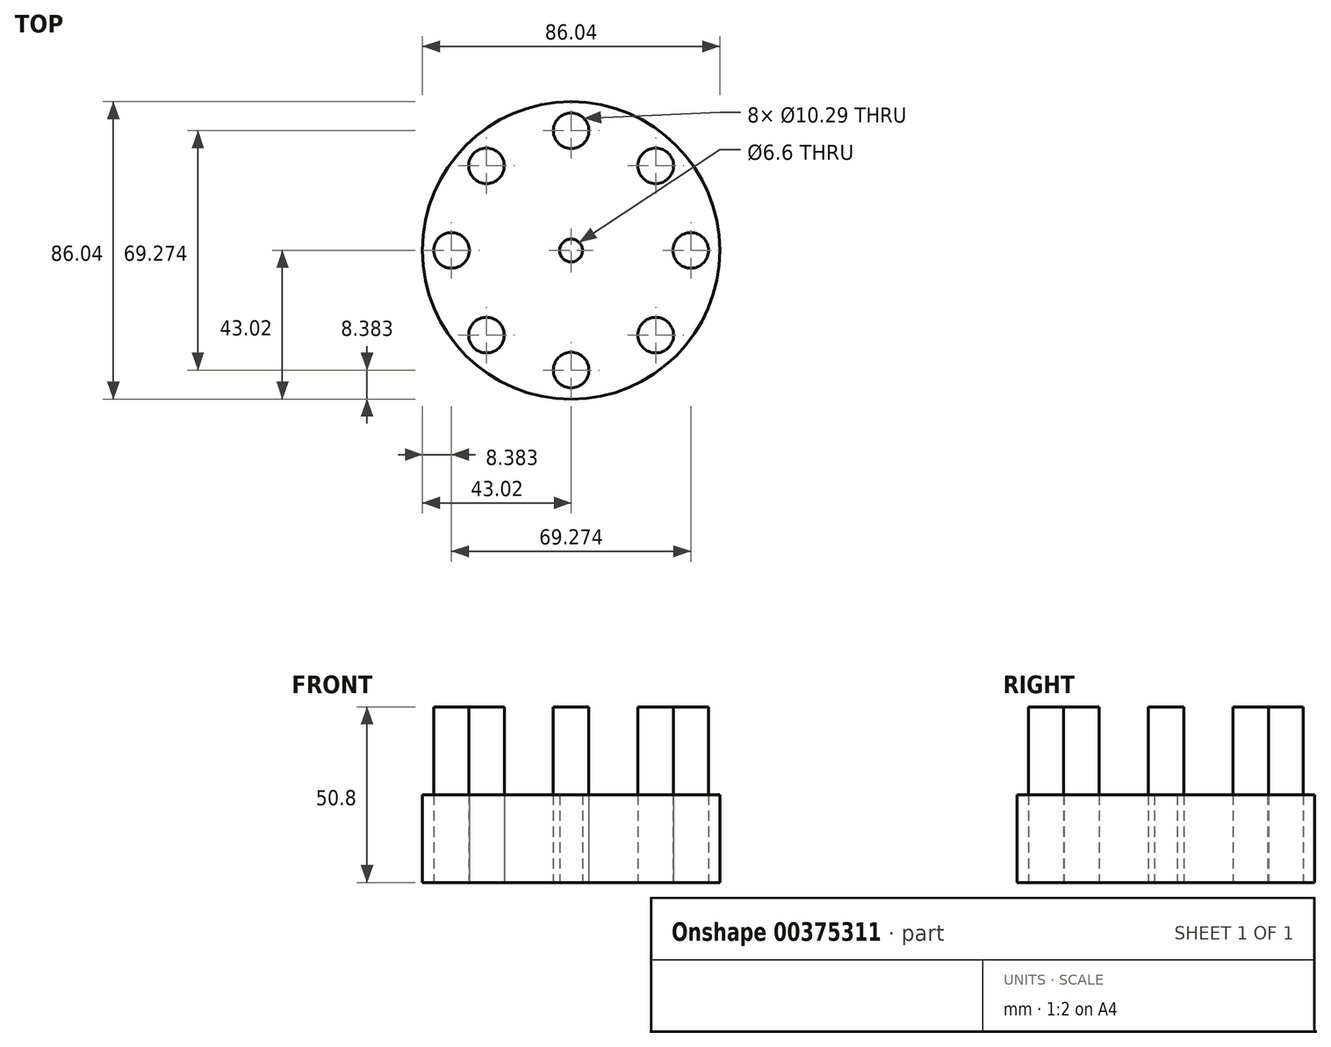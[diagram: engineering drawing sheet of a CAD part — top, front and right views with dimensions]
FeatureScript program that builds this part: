
annotation { "Feature Type Name" : "Feature", "Feature Type Description" : "" }
export const myFeature = defineFeature(function(context is Context, id is Id, definition is map)
    precondition{}
    {
        {
            var Q0;
            Q0=qCreatedBy(makeId("Top.planeOp"),FACE);
            var sketch = newSketch(context, id + "F0", { "sketchPlane" : qUnion([Q0])});
            skCircle(sketch, "E0", {"center": v(0, 0) * mm, "radius": 43.02 * mm});
            skLineSegment(sketch, "E1", {"start": v(0, 43.02) * mm, "end": v(0, 34.64) * mm, "construction": true});
            skCircle(sketch, "E2", {"center": v(0, 34.64) * mm, "radius": 5.15 * mm});
            skCircle(sketch, "E3.1.0", {"center": v(-24.5, 24.5) * mm, "radius": 5.15 * mm});
            skCircle(sketch, "E3.2.0", {"center": v(-34.64, 0) * mm, "radius": 5.15 * mm});
            skCircle(sketch, "E3.3.0", {"center": v(-24.5, -24.5) * mm, "radius": 5.15 * mm});
            skCircle(sketch, "E3.4.0", {"center": v(0, -34.64) * mm, "radius": 5.15 * mm});
            skCircle(sketch, "E3.5.0", {"center": v(24.5, -24.5) * mm, "radius": 5.15 * mm});
            skCircle(sketch, "E3.6.0", {"center": v(34.64, 0) * mm, "radius": 5.15 * mm});
            skCircle(sketch, "E3.7.0", {"center": v(24.5, 24.5) * mm, "radius": 5.15 * mm});
            skCircle(sketch, "E4", {"center": v(0, 0) * mm, "radius": 3.3 * mm});
            skSolve(sketch);
        }
        {
            var Q0;
            Q0=makeQuery(id+"F0.imprint","IMPRINT",FACE,{"disambiguationData":[TD([[makeQuery(id+"F0.imprint","IMPRINT",EDGE,{"derivedFrom":sQuery(id+"F0.wireOp",EDGE,"E2")}),1.0]])]});
            extrude(context, id + "F1", {"entities" : qUnion([Q0]), "depth" : 50.8 * mm});
        }
        {
            var Q0;
            Q0=makeQuery(id+"F0.imprint","IMPRINT",FACE,{"disambiguationData":[TD([[makeQuery(id+"F0.imprint","IMPRINT",EDGE,{"derivedFrom":sQuery(id+"F0.wireOp",EDGE,"E3.1.0")}),1.0]])]});
            extrude(context, id + "F2", {"entities" : qUnion([Q0]), "depth" : 50.8 * mm});
        }
        {
            var Q0;
            Q0=makeQuery(id+"F0.imprint","IMPRINT",FACE,{"disambiguationData":[TD([[makeQuery(id+"F0.imprint","IMPRINT",EDGE,{"derivedFrom":sQuery(id+"F0.wireOp",EDGE,"E3.2.0")}),1.0]])]});
            extrude(context, id + "F3", {"entities" : qUnion([Q0]), "depth" : 50.8 * mm});
        }
        {
            var Q0;
            Q0=makeQuery(id+"F0.imprint","IMPRINT",FACE,{"disambiguationData":[TD([[makeQuery(id+"F0.imprint","IMPRINT",EDGE,{"derivedFrom":sQuery(id+"F0.wireOp",EDGE,"E3.3.0")}),1.0]])]});
            extrude(context, id + "F4", {"entities" : qUnion([Q0]), "depth" : 50.8 * mm});
        }
        {
            var Q0;
            Q0=makeQuery(id+"F0.imprint","IMPRINT",FACE,{"disambiguationData":[TD([[makeQuery(id+"F0.imprint","IMPRINT",EDGE,{"derivedFrom":sQuery(id+"F0.wireOp",EDGE,"E3.4.0")}),1.0]])]});
            extrude(context, id + "F5", {"entities" : qUnion([Q0]), "depth" : 50.8 * mm});
        }
        {
            var Q0;
            Q0=makeQuery(id+"F0.imprint","IMPRINT",FACE,{"disambiguationData":[TD([[makeQuery(id+"F0.imprint","IMPRINT",EDGE,{"derivedFrom":sQuery(id+"F0.wireOp",EDGE,"E3.5.0")}),1.0]])]});
            extrude(context, id + "F6", {"entities" : qUnion([Q0]), "depth" : 50.8 * mm});
        }
        {
            var Q0;
            Q0=makeQuery(id+"F0.imprint","IMPRINT",FACE,{"disambiguationData":[TD([[makeQuery(id+"F0.imprint","IMPRINT",EDGE,{"derivedFrom":sQuery(id+"F0.wireOp",EDGE,"E3.6.0")}),1.0]])]});
            extrude(context, id + "F7", {"entities" : qUnion([Q0]), "depth" : 50.8 * mm});
        }
        {
            var Q0;
            Q0=makeQuery(id+"F0.imprint","IMPRINT",FACE,{"disambiguationData":[TD([[makeQuery(id+"F0.imprint","IMPRINT",EDGE,{"derivedFrom":sQuery(id+"F0.wireOp",EDGE,"E3.7.0")}),1.0]])]});
            extrude(context, id + "F8", {"entities" : qUnion([Q0]), "depth" : 50.8 * mm});
        }
        {
            var Q0;
            Q0=makeQuery(id+"F0.imprint","IMPRINT",FACE,{"disambiguationData":[TD([[makeQuery(id+"F0.imprint","IMPRINT",EDGE,{"derivedFrom":sQuery(id+"F0.wireOp",EDGE,"E0")}),1.0]])]});
            extrude(context, id + "F9", {"entities" : qUnion([Q0]), "depth" : 25.4 * mm});
        }
    });
